# Revit family: Domotics-DomesticRanges-GEWISS-SYSTEM_POWER-SOCKET-OUTLET_ITA_P11_10A
name_source: partatom
category: Apparecchi elettrici
revit_build: Autodesk Revit 2016 (Build: 20161004_0715(x64)
units: mm (PartAtom-declared; Revit-internal decimal feet)

## family parameters
Condiviso = Sì
Host = Superficie
Mantenere orientamento annotazione = Sì
Numero OmniClass = 23.80.50.14
Punto di calcolo locali = Sì
Quota connettore circolare = Usa diametro
Taglio con vuoti quando caricato = No
Tipo di parte = Normale
Titolo OmniClass = Plug Connectors

## types (2) — shared parameters
Carico apparente = 0 VA
Catalogue = DOMOTICS
Catalogue Range = SYSTEM - DOMESTIC RANGE
Characteristics = 2P+E - 10A
Description. = Socket-outlet 10 A
Description: = 2P+E - 10A
Electrocod = 0131
For plug pins = Ã˜ 4 mm
IDF = 0305239d-20ce-4581-94dd-d6e07f155f13
IDT = b8c0c6aa-2110-498c-a181-906f4d06996c
Immagine tipo = gw21201.jpg
Larghezza presa = 23 mm  [stored 0.0754593 ft]
N. poli = 2
No. SYSTEM modules = 1
Produttore = GEWISS S.p.A.
Prospetto di default = 1219 mm
Pulsante = GEWISS NERO
SEO = Socket outlet
Simbolo = SIMBOLO PRESE : PRESA
Standard = English
Standard: = English
Technical sheet = https://www.gewiss.com
Type = P11
URL = https://www.gewiss.com
Version file RFA = 19.4
Volt = 230 V
Voltage = 250 V ac
Voltage: = 250 V ac

## per-type parameters (varying)
| type | Colour | Descrizione | EAN code | Modello |
| GW20201 - 10A 2P+E italian socket outlet white | White | 10A 2P+E ITALIAN SOCKET OUTLET SY/WT | 8011564000513 | GW20201 |
| GW21201 - 10A 2P+E italian socket outlet black | Black | 10A 2P+E ITALIAN SOCKET OUTLET SY/BK | 8011564128378 | GW21201 |

note: [stored X ft] marks values corroborated as IEEE doubles in the binary element streams (Revit-internal decimal feet)

## geometry (parser evidence)
native form markers: Sweep x1
no freeform markers — native parametric forms only
